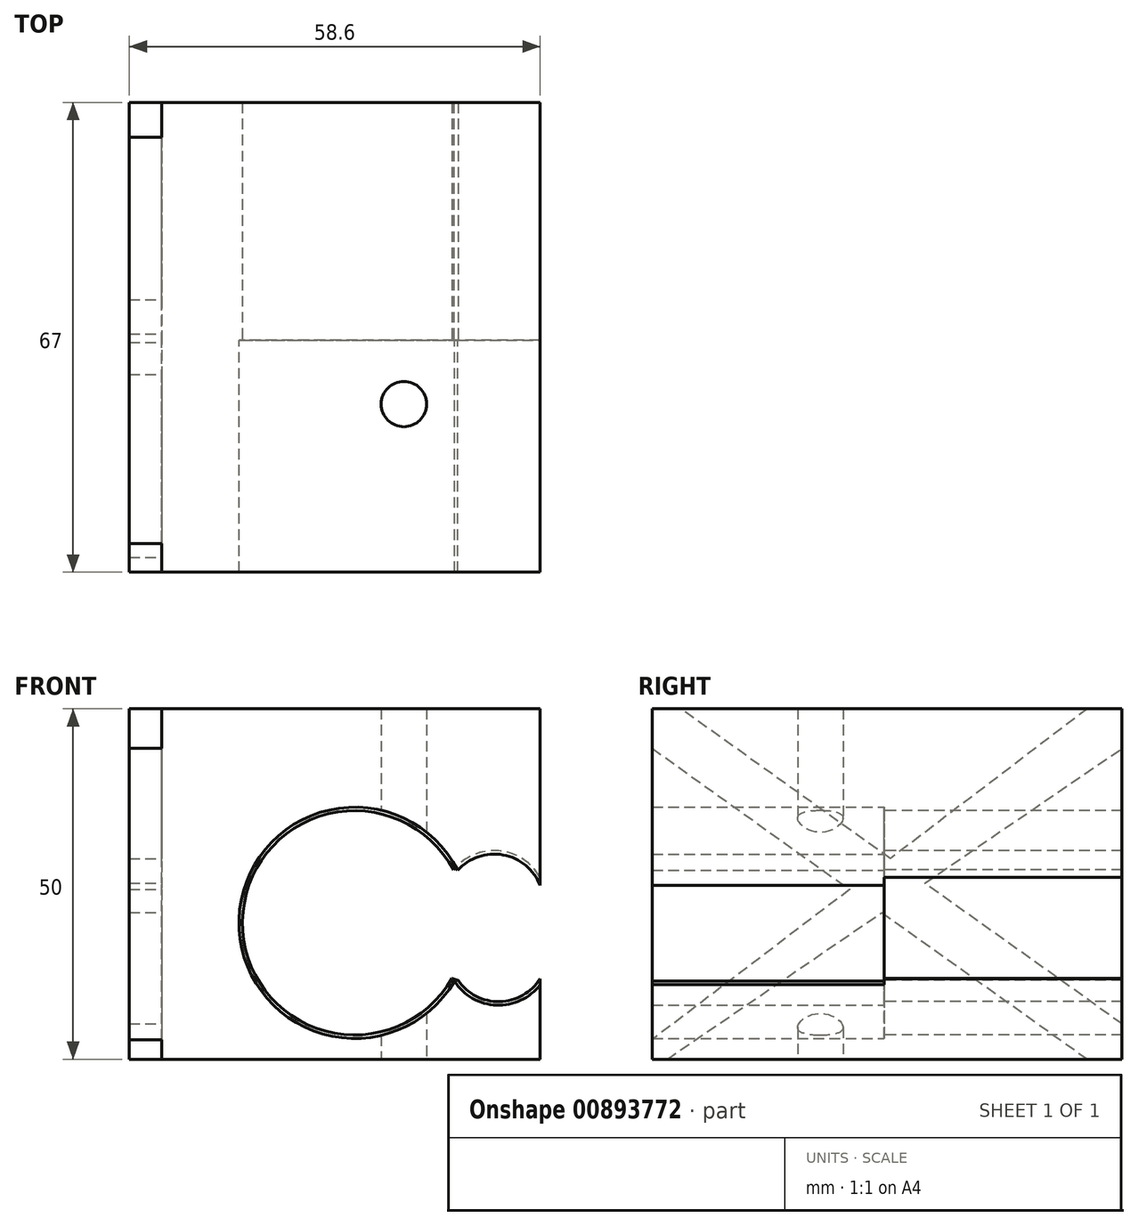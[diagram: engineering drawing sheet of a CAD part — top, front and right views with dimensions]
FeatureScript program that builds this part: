
annotation { "Feature Type Name" : "Feature", "Feature Type Description" : "" }
export const myFeature = defineFeature(function(context is Context, id is Id, definition is map)
    precondition{}
    {
        {
            var Q0;
            Q0=qCreatedBy(makeId("Top.planeOp"),FACE);
            var sketch = newSketch(context, id + "F0", { "sketchPlane" : qUnion([Q0])});
            skLineSegment(sketch, "E0.bottom", {"start": v(17.65, -33.09) * mm, "end": v(-36.35, -33.09) * mm});
            skLineSegment(sketch, "E0.top", {"start": v(17.65, 33.91) * mm, "end": v(-36.35, 33.91) * mm});
            skLineSegment(sketch, "E0.left", {"start": v(17.65, -33.09) * mm, "end": v(17.65, 33.91) * mm});
            skLineSegment(sketch, "E0.right", {"start": v(-36.35, -33.09) * mm, "end": v(-36.35, 33.91) * mm});
            skCircle(sketch, "E1", {"center": v(-1.78, -9.11) * mm, "radius": 3.24 * mm});
            skSolve(sketch);
        }
        {
            var Q0;
            Q0 = qSketchRegion(id + "F0", true);
            extrude(context, id + "F1", {"entities" : qUnion([Q0]), "depth" : 50 * mm, "offsetDistance" : 25 * mm});
        }
        {
            var Q0;
            Q0=qCreatedBy(makeId("Front.planeOp"),FACE);
            var sketch = newSketch(context, id + "F2", { "sketchPlane" : qUnion([Q0])});
            skCircle(sketch, "E2", {"center": v(-8.8, 19.46) * mm, "radius": 16.74 * mm});
            skCircle(sketch, "E3", {"center": v(7.9, 18.5) * mm, "radius": 7.82 * mm});
            skCircle(sketch, "E4", {"center": v(11.12, 22.27) * mm, "radius": 4.27 * mm});
            skCircle(sketch, "E5", {"center": v(11.72, 15.2) * mm, "radius": 4.5 * mm});
            skSolve(sketch);
        }
        {
            var Q0;
            Q0=sQuery(id+"F2.wireOp",VERTEX,"E2.center");
            var Q1;
            Q1=makeQuery(id+"F1.opExtrude","SWEPT_BODY",BODY,{"disambiguationData":[OSD([sQuery(id+"F0.wireOp",EDGE,"E0.bottom"),sQuery(id+"F0.wireOp",EDGE,"E0.top"),sQuery(id+"F0.wireOp",EDGE,"E0.left"),sQuery(id+"F0.wireOp",EDGE,"E0.right")])]});
            hole(context, id + "F3", {"style" : HoleStyle.SIMPLE, "endStyle" : HoleEndStyle.THROUGH, "oppositeDirection" : true, "holeDiameter" : 33 * mm, "majorDiameter" : 5 * mm, "isTappedThrough" : true, "tappedDepth" : 12 * mm, "tapClearance" : 3, "locations" : qUnion([Q0]), "scope" : qUnion([Q1])});
        }
        {
            var Q0;
            Q0=sQuery(id+"F2.wireOp",VERTEX,"E2.center");
            var Q1;
            Q1=makeQuery(id+"F1.opExtrude","SWEPT_BODY",BODY,{"disambiguationData":[OSD([sQuery(id+"F0.wireOp",EDGE,"E0.bottom"),sQuery(id+"F0.wireOp",EDGE,"E0.top"),sQuery(id+"F0.wireOp",EDGE,"E0.left"),sQuery(id+"F0.wireOp",EDGE,"E0.right")])]});
            hole(context, id + "F4", {"style" : HoleStyle.SIMPLE, "endStyle" : HoleEndStyle.THROUGH, "holeDiameter" : 32 * mm, "majorDiameter" : 5 * mm, "isTappedThrough" : true, "tappedDepth" : 12 * mm, "tapClearance" : 3, "locations" : qUnion([Q0]), "scope" : qUnion([Q1])});
        }
        {
            var Q0;
            Q0=sQuery(id+"F2.wireOp",VERTEX,"E4.center");
            var Q1;
            Q1=makeQuery(id+"F1.opExtrude","SWEPT_BODY",BODY,{"disambiguationData":[OSD([sQuery(id+"F0.wireOp",EDGE,"E0.bottom"),sQuery(id+"F0.wireOp",EDGE,"E0.top"),sQuery(id+"F0.wireOp",EDGE,"E0.left"),sQuery(id+"F0.wireOp",EDGE,"E0.right")])]});
            hole(context, id + "F5", {"style" : HoleStyle.SIMPLE, "endStyle" : HoleEndStyle.THROUGH, "oppositeDirection" : true, "holeDiameter" : 14 * mm, "majorDiameter" : 5 * mm, "isTappedThrough" : true, "tappedDepth" : 12 * mm, "tapClearance" : 3, "locations" : qUnion([Q0]), "scope" : qUnion([Q1])});
        }
        {
            var Q0;
            Q0=sQuery(id+"F2.wireOp",VERTEX,"E5.center");
            var Q1;
            Q1=makeQuery(id+"F1.opExtrude","SWEPT_BODY",BODY,{"disambiguationData":[OSD([sQuery(id+"F0.wireOp",EDGE,"E0.bottom"),sQuery(id+"F0.wireOp",EDGE,"E0.top"),sQuery(id+"F0.wireOp",EDGE,"E0.left"),sQuery(id+"F0.wireOp",EDGE,"E0.right")])]});
            hole(context, id + "F6", {"style" : HoleStyle.SIMPLE, "endStyle" : HoleEndStyle.THROUGH, "holeDiameter" : 14 * mm, "majorDiameter" : 5 * mm, "isTappedThrough" : true, "tappedDepth" : 12 * mm, "tapClearance" : 3, "locations" : qUnion([Q0]), "scope" : qUnion([Q1])});
        }
        {
            var Q0;
            Q0=sQuery(id+"F2.wireOp",VERTEX,"E3.center");
            var Q1;
            Q1=makeQuery(id+"F1.opExtrude","SWEPT_BODY",BODY,{"disambiguationData":[OSD([sQuery(id+"F0.wireOp",EDGE,"E0.bottom"),sQuery(id+"F0.wireOp",EDGE,"E0.top"),sQuery(id+"F0.wireOp",EDGE,"E0.left"),sQuery(id+"F0.wireOp",EDGE,"E0.right")])]});
            hole(context, id + "F7", {"style" : HoleStyle.SIMPLE, "endStyle" : HoleEndStyle.THROUGH, "oppositeDirection" : true, "holeDiameter" : 14 * mm, "majorDiameter" : 5 * mm, "isTappedThrough" : true, "tappedDepth" : 12 * mm, "tapClearance" : 3, "locations" : qUnion([Q0]), "scope" : qUnion([Q1])});
        }
        {
            var Q0;
            Q0=sQuery(id+"F2.wireOp",VERTEX,"E5.center");
            var Q1;
            Q1=makeQuery(id+"F1.opExtrude","SWEPT_BODY",BODY,{"disambiguationData":[OSD([sQuery(id+"F0.wireOp",EDGE,"E0.bottom"),sQuery(id+"F0.wireOp",EDGE,"E0.top"),sQuery(id+"F0.wireOp",EDGE,"E0.left"),sQuery(id+"F0.wireOp",EDGE,"E0.right")])]});
            hole(context, id + "F8", {"style" : HoleStyle.SIMPLE, "endStyle" : HoleEndStyle.THROUGH, "oppositeDirection" : true, "holeDiameter" : 15 * mm, "majorDiameter" : 5 * mm, "isTappedThrough" : true, "tappedDepth" : 12 * mm, "tapClearance" : 3, "locations" : qUnion([Q0]), "scope" : qUnion([Q1])});
        }
        {
            var Q0;
            Q0=sQuery(id+"F2.wireOp",VERTEX,"E3.center");
            var Q1;
            Q1=makeQuery(id+"F1.opExtrude","SWEPT_BODY",BODY,{"disambiguationData":[OSD([sQuery(id+"F0.wireOp",EDGE,"E0.bottom"),sQuery(id+"F0.wireOp",EDGE,"E0.top"),sQuery(id+"F0.wireOp",EDGE,"E0.left"),sQuery(id+"F0.wireOp",EDGE,"E0.right")])]});
            hole(context, id + "F9", {"style" : HoleStyle.SIMPLE, "endStyle" : HoleEndStyle.THROUGH, "holeDiameter" : 15 * mm, "majorDiameter" : 5 * mm, "isTappedThrough" : true, "tappedDepth" : 12 * mm, "tapClearance" : 3, "locations" : qUnion([Q0]), "scope" : qUnion([Q1])});
        }
        {
            var Q0;
            Q0=sQuery(id+"F2.wireOp",VERTEX,"E4.center");
            var Q1;
            Q1=makeQuery(id+"F1.opExtrude","SWEPT_BODY",BODY,{"disambiguationData":[OSD([sQuery(id+"F0.wireOp",EDGE,"E0.bottom"),sQuery(id+"F0.wireOp",EDGE,"E0.top"),sQuery(id+"F0.wireOp",EDGE,"E0.left"),sQuery(id+"F0.wireOp",EDGE,"E0.right")])]});
            hole(context, id + "F10", {"style" : HoleStyle.SIMPLE, "endStyle" : HoleEndStyle.THROUGH, "holeDiameter" : 15 * mm, "majorDiameter" : 5 * mm, "isTappedThrough" : true, "tappedDepth" : 12 * mm, "tapClearance" : 3, "locations" : qUnion([Q0]), "scope" : qUnion([Q1])});
        }
        {
            var Q0;
            Q0=makeQuery(id+"F1.opExtrude","SWEPT_FACE",FACE,{"disambiguationData":[OSD([sQuery(id+"F0.wireOp",EDGE,"E0.right")])]});
            var sketch = newSketch(context, id + "F11", { "sketchPlane" : qUnion([Q0])});
            skLineSegment(sketch, "E6", {"start": v(-33.91, 5.03) * mm, "end": v(29.04, 50) * mm});
            skLineSegment(sketch, "E7", {"start": v(29.04, 50) * mm, "end": v(33.09, 44.34) * mm});
            skLineSegment(sketch, "E8", {"start": v(33.09, 44.34) * mm, "end": v(-28.99, 0) * mm});
            skLineSegment(sketch, "E9", {"start": v(-28.99, 0) * mm, "end": v(-33.91, 5.03) * mm});
            skLineSegment(sketch, "E10", {"start": v(-28.99, 50) * mm, "end": v(33.09, 2.8) * mm});
            skLineSegment(sketch, "E11", {"start": v(33.09, 2.8) * mm, "end": v(30.96, 0) * mm});
            skLineSegment(sketch, "E12", {"start": v(30.96, 0) * mm, "end": v(-33.91, 44.34) * mm});
            skLineSegment(sketch, "E13", {"start": v(-33.91, 44.34) * mm, "end": v(-28.99, 50) * mm});
            skLineSegment(sketch, "E14", {"start": v(-28.99, 0) * mm, "end": v(30.96, 0) * mm});
            skLineSegment(sketch, "E15", {"start": v(33.09, 2.8) * mm, "end": v(33.09, 44.34) * mm});
            skLineSegment(sketch, "E16", {"start": v(29.04, 50) * mm, "end": v(-28.99, 50) * mm});
            skLineSegment(sketch, "E17", {"start": v(-33.91, 44.34) * mm, "end": v(-33.91, 5.03) * mm});
            skSolve(sketch);
        }
        {
            var Q0;
            {var subQ0=sQuery(id+"F11.wireOp",EDGE,"E16");Q0=makeQuery(id+"F11.imprint","IMPRINT",FACE,{"disambiguationData":[TD([[makeQuery(id+"F11.imprint","IMPRINT",EDGE,{"derivedFrom":subQ0}),1.0]])]});}
            var Q1;
            {var subQ0=sQuery(id+"F11.wireOp",EDGE,"E17");Q1=makeQuery(id+"F11.imprint","IMPRINT",FACE,{"disambiguationData":[TD([[makeQuery(id+"F11.imprint","IMPRINT",EDGE,{"derivedFrom":subQ0}),1.0]])]});}
            var Q2;
            {var subQ0=sQuery(id+"F11.wireOp",EDGE,"E15");Q2=makeQuery(id+"F11.imprint","IMPRINT",FACE,{"disambiguationData":[TD([[makeQuery(id+"F11.imprint","IMPRINT",EDGE,{"derivedFrom":subQ0}),-1.0]])]});}
            var Q3;
            {var subQ0=sQuery(id+"F11.wireOp",EDGE,"E14");Q3=makeQuery(id+"F11.imprint","IMPRINT",FACE,{"disambiguationData":[TD([[makeQuery(id+"F11.imprint","IMPRINT",EDGE,{"derivedFrom":subQ0}),-1.0]])]});}
            extrude(context, id + "F12", {"entities" : qUnion([Q0, Q1, Q2, Q3]), "operationType" : NewBodyOperationType.ADD, "depth" : 4.6 * mm, "offsetDistance" : 25 * mm});
        }
    });
